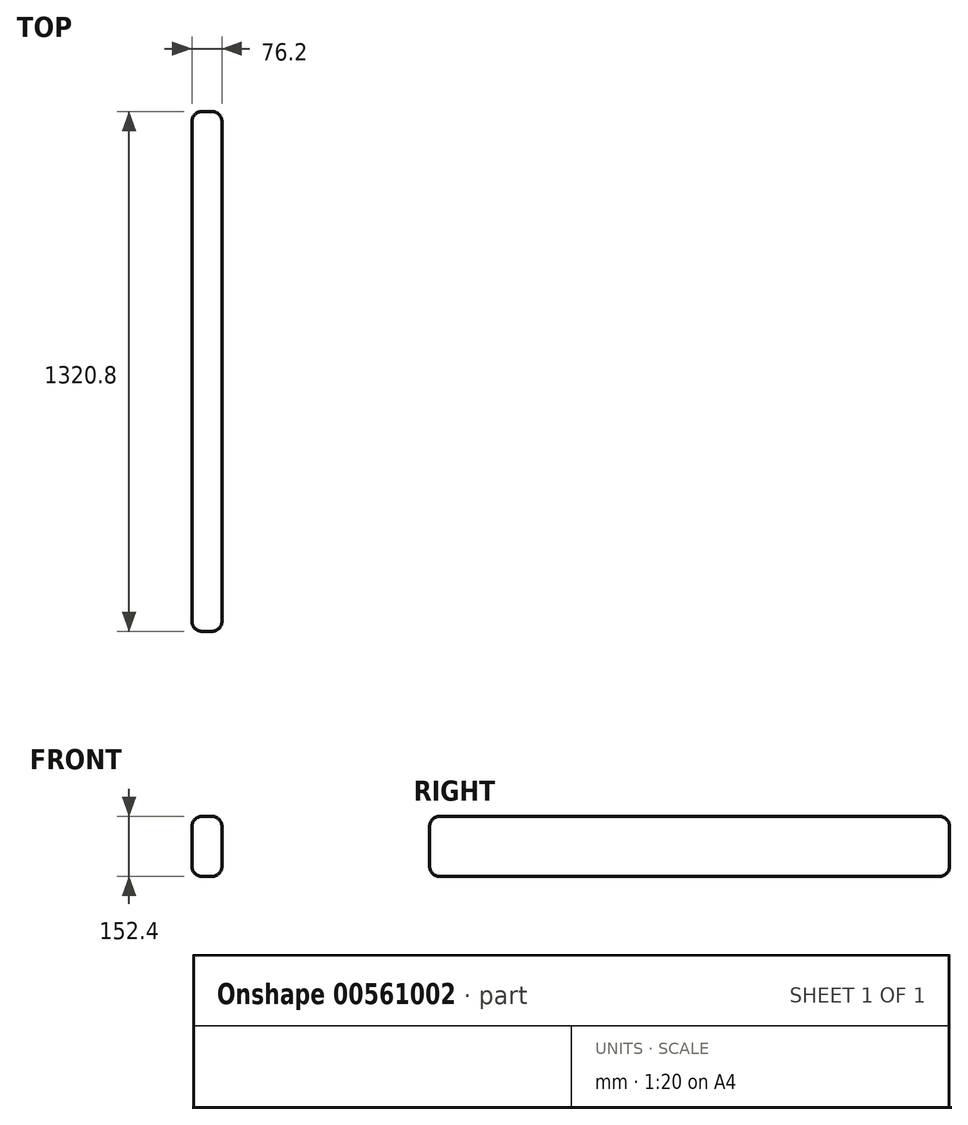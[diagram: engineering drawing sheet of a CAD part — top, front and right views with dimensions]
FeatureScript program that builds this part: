
annotation { "Feature Type Name" : "Feature", "Feature Type Description" : "" }
export const myFeature = defineFeature(function(context is Context, id is Id, definition is map)
    precondition{}
    {
        {
            var Q0;
            Q0=qCreatedBy(makeId("Front.planeOp"),FACE);
            var sketch = newSketch(context, id + "F0", { "sketchPlane" : qUnion([Q0])});
            skLineSegment(sketch, "E0.bottom", {"start": v(-12.7, 76.2) * mm, "end": v(12.7, 76.2) * mm});
            skLineSegment(sketch, "E0.top", {"start": v(-12.7, -76.2) * mm, "end": v(12.7, -76.2) * mm});
            skLineSegment(sketch, "E0.left", {"start": v(-38.1, 50.8) * mm, "end": v(-38.1, -50.8) * mm});
            skLineSegment(sketch, "E0.right", {"start": v(38.1, 50.8) * mm, "end": v(38.1, -50.8) * mm});
            skLineSegment(sketch, "E1", {"start": v(38.1, 76.2) * mm, "end": v(-38.1, -76.2) * mm});
            skPoint(sketch, "E2.visualSharp", {"position": v(-38.1, 76.2) * mm});
            skArc(sketch, "E2.filletArc", {"start": v(-12.7, 76.2) * mm, "mid": v(-30.66, 68.76) * mm, "end": v(-38.1, 50.8) * mm});
            skPoint(sketch, "E3.visualSharp", {"position": v(38.1, -76.2) * mm});
            skArc(sketch, "E3.filletArc", {"start": v(12.7, -76.2) * mm, "mid": v(30.66, -68.76) * mm, "end": v(38.1, -50.8) * mm});
            skPoint(sketch, "E4.visualSharp", {"position": v(-38.1, -76.2) * mm});
            skArc(sketch, "E4.filletArc", {"start": v(-38.1, -50.8) * mm, "mid": v(-30.66, -68.76) * mm, "end": v(-12.7, -76.2) * mm});
            skPoint(sketch, "E5.visualSharp", {"position": v(38.1, 76.2) * mm});
            skArc(sketch, "E5.filletArc", {"start": v(38.1, 50.8) * mm, "mid": v(30.66, 68.76) * mm, "end": v(12.7, 76.2) * mm});
            skSolve(sketch);
        }
        {
            var Q0;
            {var subQ6=sQuery(id+"F0.wireOp",EDGE,"E0.bottom");Q0=makeQuery(id+"F0.imprint","IMPRINT",FACE,{"disambiguationData":[TD([[makeQuery(id+"F0.imprint","IMPRINT",EDGE,{"derivedFrom":subQ6}),-1.0]])]});}
            var Q1;
            {var subQ6=sQuery(id+"F0.wireOp",EDGE,"E0.top");Q1=makeQuery(id+"F0.imprint","IMPRINT",FACE,{"disambiguationData":[TD([[makeQuery(id+"F0.imprint","IMPRINT",EDGE,{"derivedFrom":subQ6}),1.0]])]});}
            extrude(context, id + "F1", {"entities" : qUnion([Q0, Q1]), "depth" : 1320.8 * mm, "offsetDistance" : 25.4 * mm});
        }
        {
            var Q0;
            Q0=makeQuery(id+"F1.opExtrude","CAP_FACE",FACE,{"disambiguationData":[OSD([sQuery(id+"F0.wireOp",EDGE,"E0.bottom"),sQuery(id+"F0.wireOp",EDGE,"E0.top"),sQuery(id+"F0.wireOp",EDGE,"E0.left"),sQuery(id+"F0.wireOp",EDGE,"E0.right"),sQuery(id+"F0.wireOp",EDGE,"E2.filletArc"),sQuery(id+"F0.wireOp",EDGE,"E3.filletArc"),sQuery(id+"F0.wireOp",EDGE,"E4.filletArc"),sQuery(id+"F0.wireOp",EDGE,"E5.filletArc")])],"isStart":false});
            var Q1;
            Q1=makeQuery(id+"F1.opExtrude","CAP_FACE",FACE,{"disambiguationData":[OSD([sQuery(id+"F0.wireOp",EDGE,"E0.bottom"),sQuery(id+"F0.wireOp",EDGE,"E0.top"),sQuery(id+"F0.wireOp",EDGE,"E0.left"),sQuery(id+"F0.wireOp",EDGE,"E0.right"),sQuery(id+"F0.wireOp",EDGE,"E2.filletArc"),sQuery(id+"F0.wireOp",EDGE,"E3.filletArc"),sQuery(id+"F0.wireOp",EDGE,"E4.filletArc"),sQuery(id+"F0.wireOp",EDGE,"E5.filletArc")])],"isStart":true});
            fillet(context, id + "F2", {"entities" : qUnion([Q0, Q1]), "radius" : 25.4 * mm, "tangentPropagation" : true, "allowEdgeOverflow" : false});
        }
    });
